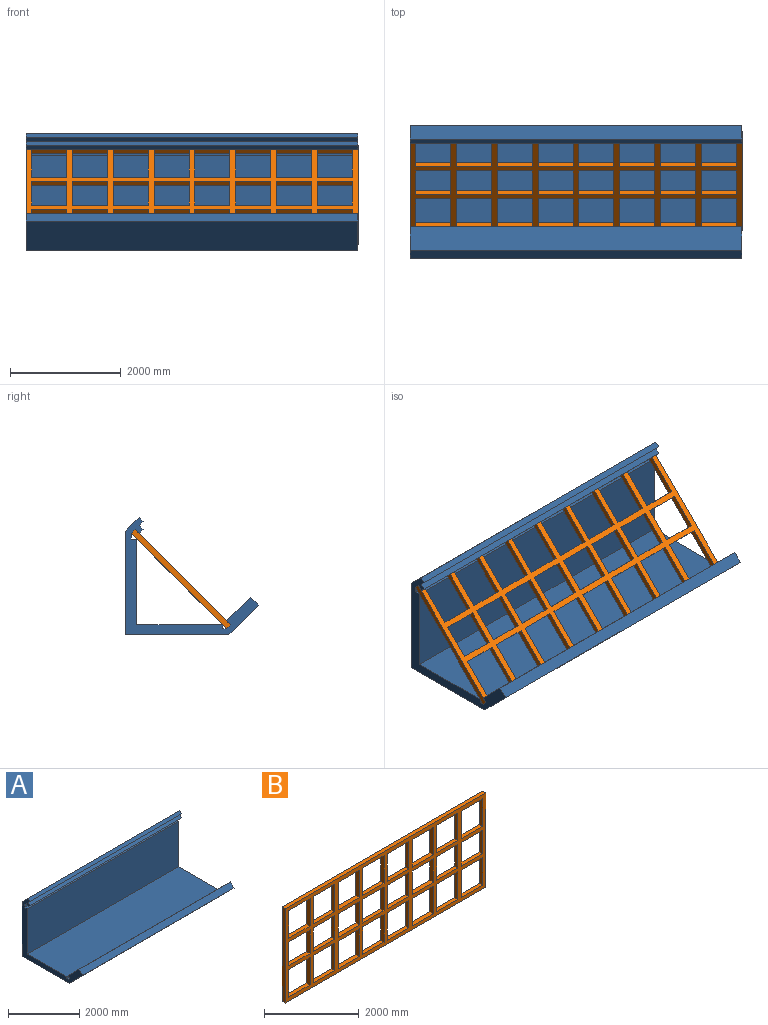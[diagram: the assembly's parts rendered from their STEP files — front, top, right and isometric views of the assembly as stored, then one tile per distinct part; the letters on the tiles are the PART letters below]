
ASSEMBLY  parts=2 mates=1
PART A: 22 faces, bbox 5994.4x2400.5x2113.2 mm
  f0: plane 5994.4x143.68mm, normal (0,-0.71,0.71), area 1218062.1mm2, adj f1,f19,f20,f21
  f1: plane 5994.4x532.65mm, normal (0,-0.71,-0.71), area 4515486.2mm2, adj f0,f2,f20,f21
  f2: plane 5994.4x1867.89mm, normal (0,0,-1), area 11196899.4mm2, adj f1,f3,f20,f21
  f3: plane 5994.4x1867.89mm, normal (0,1,0), area 11196899.4mm2, adj f2,f4,f20,f21
  f4: plane 5994.4x245.28mm, normal (0,0.71,0.71), area 2079362mm2, adj f3,f5,f20,f21
  f5: plane 5994.4x71.84mm, normal (0,-0.71,0.71), area 609031mm2, adj f4,f6,f20,f21
  f6: plane 5994.4x71.84mm, normal (0,-0.71,-0.71), area 609031mm2, adj f5,f7,f20,f21
  f7: plane 5994.4x71.84mm, normal (0,-0.71,0.71), area 609031mm2, adj f6,f8,f20,f21
  f8: plane 5994.4x71.84mm, normal (0,-0.71,-0.71), area 609031mm2, adj f7,f9,f20,f21
  f9: plane 5994.4x71.84mm, normal (0,0.71,-0.71), area 609031mm2, adj f8,f10,f20,f21
  f10: plane 5994.4x71.84mm, normal (0,-0.71,-0.71), area 609031mm2, adj f9,f11,f20,f21
  f11: plane 5994.4x101.6mm, normal (0,-1,0), area 609031mm2, adj f10,f12,f20,f21
  f12: plane 5994.4x101.6mm, normal (0,0,1), area 609031mm2, adj f11,f13,f20,f21
  f13: plane 5994.4x1550.77mm, normal (0,-1,0), area 9295918.5mm2, adj f12,f14,f20,f21
  f14: plane 5994.4x1550.77mm, normal (0,0,1), area 9295918.5mm2, adj f13,f15,f20,f21
  f15: plane 5994.4x71.84mm, normal (0,-1,0), area 430650mm2, adj f14,f16,f20,f21
  f16: plane 5994.4x71.84mm, normal (0,0,1), area 430650mm2, adj f15,f17,f20,f21
  f17: plane 5994.4x71.84mm, normal (0,0.71,0.71), area 609031mm2, adj f16,f18,f20,f21
  f18: plane 5994.4x71.84mm, normal (0,0.71,-0.71), area 609031mm2, adj f17,f19,f20,f21
  f19: plane 5994.4x431.05mm, normal (0,0.71,0.71), area 3654186.2mm2, adj f0,f18,f20,f21
  f20: plane 2400.55x2113.18mm, normal (1,0,0), area 820984.3mm2, adj f0,f1,f2,f3,f4,f5,f6,f7
  f21: plane 2400.55x2113.18mm, normal (-1,0,0), area 820984.3mm2, adj f0,f1,f2,f3,f4,f5,f6,f7
PART B: 102 faces, bbox 5994.4x101.6x2438.4 mm
  f0: plane 609.6x101.6mm, normal (-1,0,0), area 61935.4mm2, adj f54,f55,f70,f87
  f1: plane 609.6x101.6mm, normal (1,0,0), area 61935.4mm2, adj f54,f55,f85,f101
  f2: plane 609.6x101.6mm, normal (-1,0,0), area 61935.4mm2, adj f54,f55,f85,f101
  f3: plane 609.6x101.6mm, normal (1,0,0), area 61935.4mm2, adj f54,f55,f82,f99
  f4: plane 609.6x101.6mm, normal (-1,0,0), area 61935.4mm2, adj f54,f55,f82,f99
  f5: plane 609.6x101.6mm, normal (1,0,0), area 61935.4mm2, adj f54,f55,f80,f97
  f6: plane 609.6x101.6mm, normal (-1,0,0), area 61935.4mm2, adj f54,f55,f80,f97
  f7: plane 609.6x101.6mm, normal (1,0,0), area 61935.4mm2, adj f54,f55,f78,f95
  f8: plane 609.6x101.6mm, normal (-1,0,0), area 61935.4mm2, adj f54,f55,f78,f95
  f9: plane 609.6x101.6mm, normal (1,0,0), area 61935.4mm2, adj f54,f55,f76,f93
  f10: plane 609.6x101.6mm, normal (-1,0,0), area 61935.4mm2, adj f54,f55,f76,f93
  f11: plane 609.6x101.6mm, normal (1,0,0), area 61935.4mm2, adj f54,f55,f74,f91
  f12: plane 609.6x101.6mm, normal (-1,0,0), area 61935.4mm2, adj f54,f55,f74,f91
  f13: plane 609.6x101.6mm, normal (1,0,0), area 61935.4mm2, adj f54,f55,f72,f89
  f14: plane 609.6x101.6mm, normal (-1,0,0), area 61935.4mm2, adj f54,f55,f72,f89
  f15: plane 609.6x101.6mm, normal (1,0,0), area 61935.4mm2, adj f54,f55,f70,f87
  f16: plane 711.2x101.6mm, normal (-1,0,0), area 72257.9mm2, adj f46,f54,f55,f71
  f17: plane 711.2x101.6mm, normal (1,0,0), area 72257.9mm2, adj f44,f54,f55,f84
  f18: plane 711.2x101.6mm, normal (-1,0,0), area 72257.9mm2, adj f44,f54,f55,f84
  f19: plane 711.2x101.6mm, normal (1,0,0), area 72257.9mm2, adj f42,f54,f55,f83
  f20: plane 711.2x101.6mm, normal (-1,0,0), area 72257.9mm2, adj f42,f54,f55,f83
  f21: plane 711.2x101.6mm, normal (1,0,0), area 72257.9mm2, adj f40,f54,f55,f81
  f22: plane 711.2x101.6mm, normal (-1,0,0), area 72257.9mm2, adj f40,f54,f55,f81
  f23: plane 711.2x101.6mm, normal (1,0,0), area 72257.9mm2, adj f38,f54,f55,f79
  f24: plane 711.2x101.6mm, normal (-1,0,0), area 72257.9mm2, adj f38,f54,f55,f79
  f25: plane 711.2x101.6mm, normal (1,0,0), area 72257.9mm2, adj f36,f54,f55,f77
  f26: plane 711.2x101.6mm, normal (-1,0,0), area 72257.9mm2, adj f36,f54,f55,f77
  f27: plane 711.2x101.6mm, normal (1,0,0), area 72257.9mm2, adj f34,f54,f55,f75
  f28: plane 711.2x101.6mm, normal (-1,0,0), area 72257.9mm2, adj f34,f54,f55,f75
  f29: plane 711.2x101.6mm, normal (1,0,0), area 72257.9mm2, adj f32,f54,f55,f73
  f30: plane 711.2x101.6mm, normal (-1,0,0), area 72257.9mm2, adj f32,f54,f55,f73
  f31: plane 711.2x101.6mm, normal (1,0,0), area 72257.9mm2, adj f46,f54,f55,f71
  f32: plane 635x101.6mm, normal (0,0,-1), area 64516mm2, adj f29,f30,f54,f55
  f33: plane 635x101.6mm, normal (0,0,1), area 64516mm2, adj f54,f55,f67,f68
  f34: plane 635x101.6mm, normal (0,0,-1), area 64516mm2, adj f27,f28,f54,f55
  f35: plane 635x101.6mm, normal (0,0,1), area 64516mm2, adj f54,f55,f65,f66
  f36: plane 635x101.6mm, normal (0,0,-1), area 64516mm2, adj f25,f26,f54,f55
  f37: plane 635x101.6mm, normal (0,0,1), area 64516mm2, adj f54,f55,f63,f64
  f38: plane 635x101.6mm, normal (0,0,-1), area 64516mm2, adj f23,f24,f54,f55
  f39: plane 635x101.6mm, normal (0,0,1), area 64516mm2, adj f54,f55,f61,f62
  f40: plane 635x101.6mm, normal (0,0,-1), area 64516mm2, adj f21,f22,f54,f55
  f41: plane 635x101.6mm, normal (0,0,1), area 64516mm2, adj f54,f55,f59,f60
  f42: plane 635x101.6mm, normal (0,0,-1), area 64516mm2, adj f19,f20,f54,f55
  f43: plane 635x101.6mm, normal (0,0,1), area 64516mm2, adj f54,f55,f57,f58
  f44: plane 635x101.6mm, normal (0,0,-1), area 64516mm2, adj f17,f18,f54,f55
  f45: plane 635x101.6mm, normal (0,0,1), area 64516mm2, adj f53,f54,f55,f56
  f46: plane 635x101.6mm, normal (0,0,-1), area 64516mm2, adj f16,f31,f54,f55
  f47: plane 711.2x101.6mm, normal (-1,0,0), area 72257.9mm2, adj f48,f54,f55,f86
  f48: plane 635x101.6mm, normal (0,0,1), area 64516mm2, adj f47,f54,f55,f69
  f49: plane 2438.4x101.6mm, normal (1,0,0), area 247741.4mm2, adj f50,f52,f54,f55
  f50: plane 5994.4x101.6mm, normal (0,0,1), area 609031mm2, adj f49,f51,f54,f55
  f51: plane 2438.4x101.6mm, normal (-1,0,0), area 247741.4mm2, adj f50,f52,f54,f55
  f52: plane 5994.4x101.6mm, normal (0,0,-1), area 609031mm2, adj f49,f51,f54,f55
  f53: plane 711.2x101.6mm, normal (1,0,0), area 72257.9mm2, adj f45,f54,f55,f100
  f54: plane 5994.4x2438.4mm, normal (0,-1,0), area 4294185mm2, adj f0,f1,f2,f3,f4,f5,f6,f7
  f55: plane 5994.4x2438.4mm, normal (0,1,0), area 4294185mm2, adj f0,f1,f2,f3,f4,f5,f6,f7
  f56: plane 711.2x101.6mm, normal (-1,0,0), area 72257.9mm2, adj f45,f54,f55,f100
  f57: plane 711.2x101.6mm, normal (1,0,0), area 72257.9mm2, adj f43,f54,f55,f98
  f58: plane 711.2x101.6mm, normal (-1,0,0), area 72257.9mm2, adj f43,f54,f55,f98
  f59: plane 711.2x101.6mm, normal (1,0,0), area 72257.9mm2, adj f41,f54,f55,f96
  f60: plane 711.2x101.6mm, normal (-1,0,0), area 72257.9mm2, adj f41,f54,f55,f96
  f61: plane 711.2x101.6mm, normal (1,0,0), area 72257.9mm2, adj f39,f54,f55,f94
  f62: plane 711.2x101.6mm, normal (-1,0,0), area 72257.9mm2, adj f39,f54,f55,f94
  f63: plane 711.2x101.6mm, normal (1,0,0), area 72257.9mm2, adj f37,f54,f55,f92
  f64: plane 711.2x101.6mm, normal (-1,0,0), area 72257.9mm2, adj f37,f54,f55,f92
  f65: plane 711.2x101.6mm, normal (1,0,0), area 72257.9mm2, adj f35,f54,f55,f90
  f66: plane 711.2x101.6mm, normal (-1,0,0), area 72257.9mm2, adj f35,f54,f55,f90
  f67: plane 711.2x101.6mm, normal (1,0,0), area 72257.9mm2, adj f33,f54,f55,f88
  f68: plane 711.2x101.6mm, normal (-1,0,0), area 72257.9mm2, adj f33,f54,f55,f88
  f69: plane 711.2x101.6mm, normal (1,0,0), area 72257.9mm2, adj f48,f54,f55,f86
  f70: plane 635x101.6mm, normal (0,0,-1), area 64516mm2, adj f0,f15,f54,f55
  f71: plane 635x101.6mm, normal (0,0,1), area 64516mm2, adj f16,f31,f54,f55
  f72: plane 635x101.6mm, normal (0,0,-1), area 64516mm2, adj f13,f14,f54,f55
  f73: plane 635x101.6mm, normal (0,0,1), area 64516mm2, adj f29,f30,f54,f55
  f74: plane 635x101.6mm, normal (0,0,-1), area 64516mm2, adj f11,f12,f54,f55
  f75: plane 635x101.6mm, normal (0,0,1), area 64516mm2, adj f27,f28,f54,f55
  f76: plane 635x101.6mm, normal (0,0,-1), area 64516mm2, adj f9,f10,f54,f55
  f77: plane 635x101.6mm, normal (0,0,1), area 64516mm2, adj f25,f26,f54,f55
  f78: plane 635x101.6mm, normal (0,0,-1), area 64516mm2, adj f7,f8,f54,f55
  f79: plane 635x101.6mm, normal (0,0,1), area 64516mm2, adj f23,f24,f54,f55
  f80: plane 635x101.6mm, normal (0,0,-1), area 64516mm2, adj f5,f6,f54,f55
  f81: plane 635x101.6mm, normal (0,0,1), area 64516mm2, adj f21,f22,f54,f55
  f82: plane 635x101.6mm, normal (0,0,-1), area 64516mm2, adj f3,f4,f54,f55
  f83: plane 635x101.6mm, normal (0,0,1), area 64516mm2, adj f19,f20,f54,f55
  f84: plane 635x101.6mm, normal (0,0,1), area 64516mm2, adj f17,f18,f54,f55
  f85: plane 635x101.6mm, normal (0,0,-1), area 64516mm2, adj f1,f2,f54,f55
  f86: plane 635x101.6mm, normal (0,0,-1), area 64516mm2, adj f47,f54,f55,f69
  f87: plane 635x101.6mm, normal (0,0,1), area 64516mm2, adj f0,f15,f54,f55
  f88: plane 635x101.6mm, normal (0,0,-1), area 64516mm2, adj f54,f55,f67,f68
  f89: plane 635x101.6mm, normal (0,0,1), area 64516mm2, adj f13,f14,f54,f55
  f90: plane 635x101.6mm, normal (0,0,-1), area 64516mm2, adj f54,f55,f65,f66
  f91: plane 635x101.6mm, normal (0,0,1), area 64516mm2, adj f11,f12,f54,f55
  f92: plane 635x101.6mm, normal (0,0,-1), area 64516mm2, adj f54,f55,f63,f64
  f93: plane 635x101.6mm, normal (0,0,1), area 64516mm2, adj f9,f10,f54,f55
  f94: plane 635x101.6mm, normal (0,0,-1), area 64516mm2, adj f54,f55,f61,f62
  f95: plane 635x101.6mm, normal (0,0,1), area 64516mm2, adj f7,f8,f54,f55
  f96: plane 635x101.6mm, normal (0,0,-1), area 64516mm2, adj f54,f55,f59,f60
  f97: plane 635x101.6mm, normal (0,0,1), area 64516mm2, adj f5,f6,f54,f55
  f98: plane 635x101.6mm, normal (0,0,-1), area 64516mm2, adj f54,f55,f57,f58
  f99: plane 635x101.6mm, normal (0,0,1), area 64516mm2, adj f3,f4,f54,f55
  f100: plane 635x101.6mm, normal (0,0,-1), area 64516mm2, adj f53,f54,f55,f56
  f101: plane 635x101.6mm, normal (0,0,1), area 64516mm2, adj f1,f2,f54,f55
PLACE A t=(-5994.4,42.08,101.6)mm
PLACE B rot(axis=(-1,0,0),45deg) t=(-2997.2,904.19,963.7)mm
MATE planar B.f52 <-> A.f17  axis (0,-0.71,-0.71) through (-2997.2,6.16,137.52)mm
